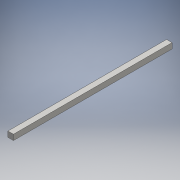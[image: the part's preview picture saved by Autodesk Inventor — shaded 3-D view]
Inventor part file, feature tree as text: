
AUTODESK INVENTOR PART (.ipt)
format: ipt  version: 2016 (Build 200138000, 138)  size: 89,088 bytes
history: native  units: mm
features: other x1, extrude x1, sketch x1
ambient origin geometry x8: Origin, YZ Plane, XZ Plane, XY Plane, X Axis, Y Axis, Z Axis, Center Point
bodies: Body1 (feature_tree)
feature tree (3):
  other  "ソリッド1"
  extrude  "押し出し1"  Depth=20.0mm
  sketch  "スケッチ1"
